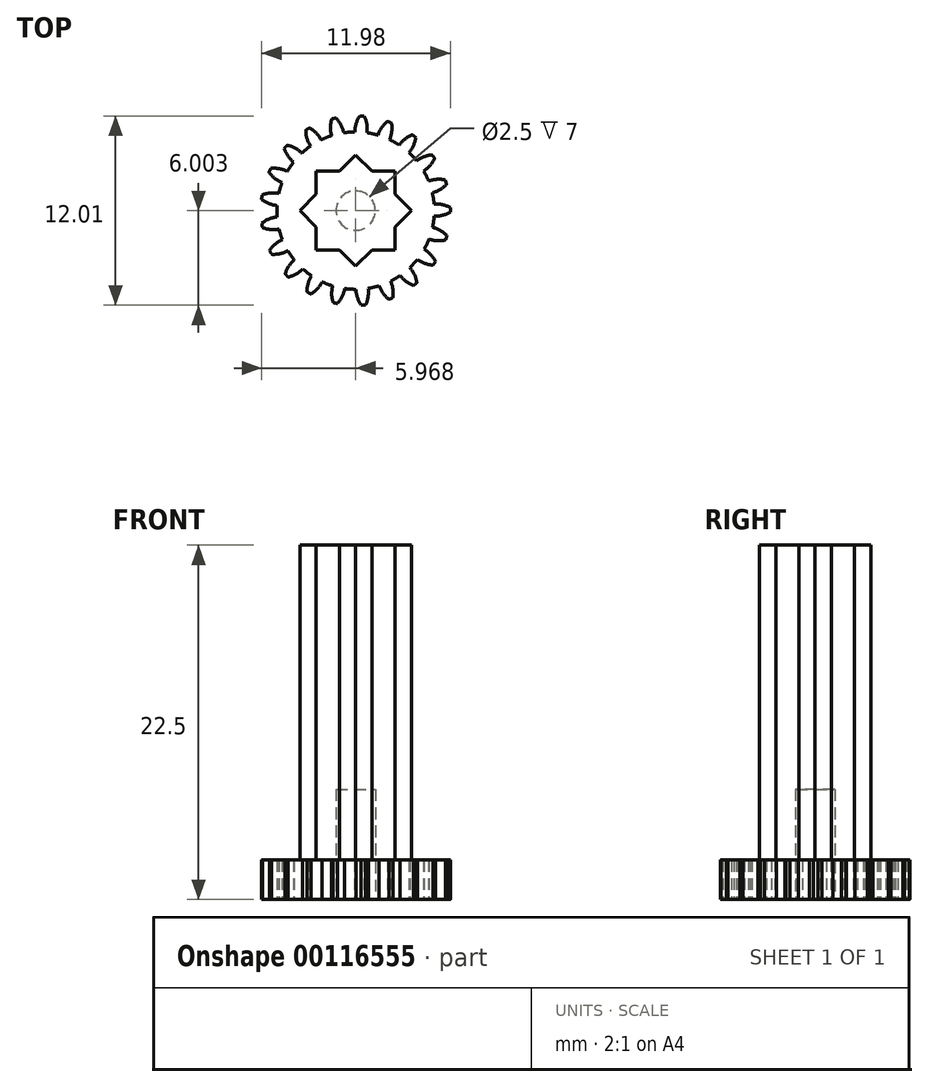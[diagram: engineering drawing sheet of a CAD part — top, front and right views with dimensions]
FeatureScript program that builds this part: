
annotation { "Feature Type Name" : "Feature", "Feature Type Description" : "" }
export const myFeature = defineFeature(function(context is Context, id is Id, definition is map)
    precondition{}
    {
        {
            var Q0;
            Q0=qCreatedBy(makeId("Top.planeOp"),FACE);
            var sketch = newSketch(context, id + "F0", { "sketchPlane" : qUnion([Q0])});
            skLineSegment(sketch, "E0", {"start": v(61.42, 3.14) * mm, "end": v(65.52, 3.14) * mm, "construction": true});
            skLineSegment(sketch, "E1", {"start": v(61.42, 3.14) * mm, "end": v(65.31, 4.4) * mm, "construction": true});
            skLineSegment(sketch, "E2", {"start": v(61.42, 3.14) * mm, "end": v(65.72, 3.82) * mm, "construction": true});
            skPoint(sketch, "E3.third.point", {"position": v(57.79, 0) * mm});
            skArc(sketch, "E4.MirrorCS", {"start": v(62.86, 3.22) * mm, "mid": v(63.38, 3.1) * mm, "end": v(63.92, 3.14) * mm});
            skArc(sketch, "E5.MirrorCS", {"start": v(62.86, 3.22) * mm, "mid": v(62.85, 3.3) * mm, "end": v(62.84, 3.36) * mm});
            skArc(sketch, "E6.MirrorCS", {"start": v(62.82, 3.5) * mm, "mid": v(62.83, 3.43) * mm, "end": v(62.84, 3.36) * mm});
            skArc(sketch, "E7.MirrorCS", {"start": v(62.82, 3.5) * mm, "mid": v(63.28, 3.78) * mm, "end": v(63.8, 3.9) * mm});
            skLineSegment(sketch, "E8", {"start": v(68.78, 4.3) * mm, "end": v(63.8, 3.9) * mm, "construction": true});
            skArc(sketch, "E9.MirrorCS", {"start": v(63.8, 4.7) * mm, "mid": v(63.78, 4.3) * mm, "end": v(63.8, 3.9) * mm});
            skArc(sketch, "E10.1.0", {"start": v(63.44, 1.53) * mm, "mid": v(63.98, 1.57) * mm, "end": v(64.48, 1.76) * mm});
            skArc(sketch, "E10.1.1", {"start": v(63.32, 1.78) * mm, "mid": v(63.35, 1.72) * mm, "end": v(63.38, 1.65) * mm});
            skArc(sketch, "E10.1.2", {"start": v(63.44, 1.53) * mm, "mid": v(63.4, 1.6) * mm, "end": v(63.38, 1.65) * mm});
            skArc(sketch, "E10.1.3", {"start": v(63.32, 1.78) * mm, "mid": v(63.68, 2.18) * mm, "end": v(64.13, 2.46) * mm});
            skArc(sketch, "E10.1.4", {"start": v(63.9, 3.2) * mm, "mid": v(64, 2.83) * mm, "end": v(64.13, 2.46) * mm});
            skArc(sketch, "E10.2.0", {"start": v(64.5, 0.08) * mm, "mid": v(65, 0.27) * mm, "end": v(65.42, 0.6) * mm});
            skArc(sketch, "E10.2.1", {"start": v(64.3, 0.28) * mm, "mid": v(64.35, 0.23) * mm, "end": v(64.4, 0.18) * mm});
            skArc(sketch, "E10.2.2", {"start": v(64.5, 0.08) * mm, "mid": v(64.45, 0.13) * mm, "end": v(64.4, 0.18) * mm});
            skArc(sketch, "E10.2.3", {"start": v(64.3, 0.28) * mm, "mid": v(64.53, 0.77) * mm, "end": v(64.88, 1.17) * mm});
            skArc(sketch, "E10.2.4", {"start": v(64.44, 1.82) * mm, "mid": v(64.65, 1.48) * mm, "end": v(64.88, 1.17) * mm});
            skArc(sketch, "E10.3.0", {"start": v(65.93, -1) * mm, "mid": v(66.35, -0.66) * mm, "end": v(66.66, -0.23) * mm});
            skArc(sketch, "E10.3.1", {"start": v(65.69, -0.86) * mm, "mid": v(65.75, -0.9) * mm, "end": v(65.8, -0.93) * mm});
            skArc(sketch, "E10.3.2", {"start": v(65.93, -1) * mm, "mid": v(65.87, -0.96) * mm, "end": v(65.8, -0.93) * mm});
            skArc(sketch, "E10.3.3", {"start": v(65.69, -0.86) * mm, "mid": v(65.76, -0.33) * mm, "end": v(65.98, 0.16) * mm});
            skArc(sketch, "E10.3.4", {"start": v(65.37, 0.65) * mm, "mid": v(65.66, 0.4) * mm, "end": v(65.98, 0.16) * mm});
            skArc(sketch, "E10.4.0", {"start": v(67.62, -1.6) * mm, "mid": v(67.92, -1.16) * mm, "end": v(68.09, -0.65) * mm});
            skArc(sketch, "E10.4.1", {"start": v(67.35, -1.54) * mm, "mid": v(67.42, -1.56) * mm, "end": v(67.48, -1.57) * mm});
            skArc(sketch, "E10.4.2", {"start": v(67.62, -1.6) * mm, "mid": v(67.55, -1.59) * mm, "end": v(67.48, -1.57) * mm});
            skArc(sketch, "E10.4.3", {"start": v(67.35, -1.54) * mm, "mid": v(67.26, -1.01) * mm, "end": v(67.32, -0.48) * mm});
            skArc(sketch, "E10.4.4", {"start": v(66.6, -0.2) * mm, "mid": v(66.95, -0.35) * mm, "end": v(67.32, -0.48) * mm});
            skArc(sketch, "E10.5.0", {"start": v(69.41, -1.68) * mm, "mid": v(69.57, -1.17) * mm, "end": v(69.58, -0.63) * mm});
            skArc(sketch, "E10.5.1", {"start": v(69.13, -1.7) * mm, "mid": v(69.2, -1.7) * mm, "end": v(69.27, -1.7) * mm});
            skArc(sketch, "E10.5.2", {"start": v(69.41, -1.68) * mm, "mid": v(69.34, -1.69) * mm, "end": v(69.27, -1.7) * mm});
            skArc(sketch, "E10.5.3", {"start": v(69.13, -1.7) * mm, "mid": v(68.9, -1.22) * mm, "end": v(68.8, -0.7) * mm});
            skArc(sketch, "E10.5.4", {"start": v(68.02, -0.64) * mm, "mid": v(68.4, -0.68) * mm, "end": v(68.8, -0.7) * mm});
            skArc(sketch, "E10.6.0", {"start": v(71.15, -1.23) * mm, "mid": v(71.15, -0.7) * mm, "end": v(71, -0.18) * mm});
            skArc(sketch, "E10.6.1", {"start": v(70.89, -1.33) * mm, "mid": v(70.95, -1.3) * mm, "end": v(71.02, -1.28) * mm});
            skArc(sketch, "E10.6.2", {"start": v(71.15, -1.23) * mm, "mid": v(71.08, -1.25) * mm, "end": v(71.02, -1.28) * mm});
            skArc(sketch, "E10.6.3", {"start": v(70.89, -1.33) * mm, "mid": v(70.52, -0.94) * mm, "end": v(70.27, -0.47) * mm});
            skArc(sketch, "E10.6.4", {"start": v(69.5, -0.64) * mm, "mid": v(69.9, -0.57) * mm, "end": v(70.27, -0.47) * mm});
            skArc(sketch, "E10.7.0", {"start": v(72.67, -0.28) * mm, "mid": v(72.51, 0.23) * mm, "end": v(72.22, 0.68) * mm});
            skArc(sketch, "E10.7.1", {"start": v(72.45, -0.46) * mm, "mid": v(72.5, -0.42) * mm, "end": v(72.56, -0.37) * mm});
            skArc(sketch, "E10.7.2", {"start": v(72.67, -0.28) * mm, "mid": v(72.62, -0.33) * mm, "end": v(72.56, -0.37) * mm});
            skArc(sketch, "E10.7.3", {"start": v(72.45, -0.46) * mm, "mid": v(71.99, -0.2) * mm, "end": v(71.61, 0.18) * mm});
            skArc(sketch, "E10.7.4", {"start": v(70.93, -0.2) * mm, "mid": v(71.28, -0.03) * mm, "end": v(71.61, 0.18) * mm});
            skArc(sketch, "E10.8.0", {"start": v(73.85, 1.07) * mm, "mid": v(73.55, 1.51) * mm, "end": v(73.14, 1.85) * mm});
            skArc(sketch, "E10.8.1", {"start": v(73.7, 0.84) * mm, "mid": v(73.73, 0.9) * mm, "end": v(73.77, 0.95) * mm});
            skArc(sketch, "E10.8.2", {"start": v(73.85, 1.07) * mm, "mid": v(73.81, 1.01) * mm, "end": v(73.77, 0.95) * mm});
            skArc(sketch, "E10.8.3", {"start": v(73.7, 0.84) * mm, "mid": v(73.17, 0.95) * mm, "end": v(72.7, 1.2) * mm});
            skArc(sketch, "E10.8.4", {"start": v(72.17, 0.63) * mm, "mid": v(72.44, 0.9) * mm, "end": v(72.7, 1.2) * mm});
            skArc(sketch, "E10.9.0", {"start": v(74.58, 2.7) * mm, "mid": v(74.16, 3.04) * mm, "end": v(73.66, 3.24) * mm});
            skArc(sketch, "E10.9.1", {"start": v(74.5, 2.44) * mm, "mid": v(74.52, 2.5) * mm, "end": v(74.54, 2.57) * mm});
            skArc(sketch, "E10.9.2", {"start": v(74.58, 2.7) * mm, "mid": v(74.56, 2.64) * mm, "end": v(74.54, 2.57) * mm});
            skArc(sketch, "E10.9.3", {"start": v(74.5, 2.44) * mm, "mid": v(73.96, 2.4) * mm, "end": v(73.44, 2.5) * mm});
            skArc(sketch, "E10.9.4", {"start": v(73.1, 1.8) * mm, "mid": v(73.28, 2.14) * mm, "end": v(73.44, 2.5) * mm});
            skArc(sketch, "E10.10.0", {"start": v(74.79, 4.49) * mm, "mid": v(74.3, 4.68) * mm, "end": v(73.76, 4.73) * mm});
            skArc(sketch, "E10.10.1", {"start": v(74.8, 4.2) * mm, "mid": v(74.8, 4.28) * mm, "end": v(74.8, 4.35) * mm});
            skArc(sketch, "E10.10.2", {"start": v(74.79, 4.49) * mm, "mid": v(74.8, 4.42) * mm, "end": v(74.8, 4.35) * mm});
            skArc(sketch, "E10.10.3", {"start": v(74.8, 4.2) * mm, "mid": v(74.3, 4) * mm, "end": v(73.77, 3.95) * mm});
            skArc(sketch, "E10.10.4", {"start": v(73.65, 3.18) * mm, "mid": v(73.72, 3.56) * mm, "end": v(73.77, 3.95) * mm});
            skArc(sketch, "E10.11.0", {"start": v(74.47, 6.25) * mm, "mid": v(73.93, 6.3) * mm, "end": v(73.41, 6.18) * mm});
            skArc(sketch, "E10.11.1", {"start": v(74.55, 5.99) * mm, "mid": v(74.53, 6.05) * mm, "end": v(74.51, 6.12) * mm});
            skArc(sketch, "E10.11.2", {"start": v(74.47, 6.25) * mm, "mid": v(74.5, 6.19) * mm, "end": v(74.51, 6.12) * mm});
            skArc(sketch, "E10.11.3", {"start": v(74.55, 5.99) * mm, "mid": v(74.14, 5.64) * mm, "end": v(73.65, 5.44) * mm});
            skArc(sketch, "E10.11.4", {"start": v(73.77, 4.66) * mm, "mid": v(73.72, 5.05) * mm, "end": v(73.65, 5.44) * mm});
            skArc(sketch, "E10.12.0", {"start": v(73.64, 7.84) * mm, "mid": v(73.12, 7.72) * mm, "end": v(72.65, 7.46) * mm});
            skArc(sketch, "E10.12.1", {"start": v(73.8, 7.61) * mm, "mid": v(73.76, 7.67) * mm, "end": v(73.72, 7.73) * mm});
            skArc(sketch, "E10.12.2", {"start": v(73.64, 7.84) * mm, "mid": v(73.68, 7.79) * mm, "end": v(73.72, 7.73) * mm});
            skArc(sketch, "E10.12.3", {"start": v(73.8, 7.61) * mm, "mid": v(73.5, 7.17) * mm, "end": v(73.1, 6.82) * mm});
            skArc(sketch, "E10.12.4", {"start": v(73.44, 6.12) * mm, "mid": v(73.28, 6.47) * mm, "end": v(73.1, 6.82) * mm});
            skArc(sketch, "E10.13.0", {"start": v(72.38, 9.12) * mm, "mid": v(71.92, 8.85) * mm, "end": v(71.55, 8.46) * mm});
            skArc(sketch, "E10.13.1", {"start": v(72.6, 8.95) * mm, "mid": v(72.55, 9) * mm, "end": v(72.5, 9.03) * mm});
            skArc(sketch, "E10.13.2", {"start": v(72.38, 9.12) * mm, "mid": v(72.44, 9.08) * mm, "end": v(72.5, 9.03) * mm});
            skArc(sketch, "E10.13.3", {"start": v(72.6, 8.95) * mm, "mid": v(72.45, 8.43) * mm, "end": v(72.16, 7.98) * mm});
            skArc(sketch, "E10.13.4", {"start": v(72.7, 7.4) * mm, "mid": v(72.44, 7.7) * mm, "end": v(72.16, 7.98) * mm});
            skArc(sketch, "E10.14.0", {"start": v(70.8, 9.97) * mm, "mid": v(70.44, 9.58) * mm, "end": v(70.2, 9.1) * mm});
            skArc(sketch, "E10.14.1", {"start": v(71.06, 9.87) * mm, "mid": v(71, 9.9) * mm, "end": v(70.93, 9.92) * mm});
            skArc(sketch, "E10.14.2", {"start": v(70.8, 9.97) * mm, "mid": v(70.87, 9.94) * mm, "end": v(70.93, 9.92) * mm});
            skArc(sketch, "E10.14.3", {"start": v(71.06, 9.87) * mm, "mid": v(71.07, 9.33) * mm, "end": v(70.93, 8.82) * mm});
            skArc(sketch, "E10.14.4", {"start": v(71.6, 8.43) * mm, "mid": v(71.28, 8.63) * mm, "end": v(70.93, 8.82) * mm});
            skArc(sketch, "E10.15.0", {"start": v(69.04, 10.31) * mm, "mid": v(68.81, 9.83) * mm, "end": v(68.72, 9.3) * mm});
            skArc(sketch, "E10.15.1", {"start": v(69.32, 10.3) * mm, "mid": v(69.25, 10.3) * mm, "end": v(69.18, 10.3) * mm});
            skArc(sketch, "E10.15.2", {"start": v(69.04, 10.31) * mm, "mid": v(69.11, 10.3) * mm, "end": v(69.18, 10.3) * mm});
            skArc(sketch, "E10.15.3", {"start": v(69.32, 10.3) * mm, "mid": v(69.49, 9.78) * mm, "end": v(69.5, 9.25) * mm});
            skArc(sketch, "E10.15.4", {"start": v(70.27, 9.08) * mm, "mid": v(69.89, 9.18) * mm, "end": v(69.5, 9.25) * mm});
            skArc(sketch, "E10.16.0", {"start": v(67.26, 10.12) * mm, "mid": v(67.18, 9.6) * mm, "end": v(67.25, 9.06) * mm});
            skArc(sketch, "E10.16.1", {"start": v(67.53, 10.19) * mm, "mid": v(67.46, 10.17) * mm, "end": v(67.4, 10.16) * mm});
            skArc(sketch, "E10.16.2", {"start": v(67.26, 10.12) * mm, "mid": v(67.33, 10.14) * mm, "end": v(67.4, 10.16) * mm});
            skArc(sketch, "E10.16.3", {"start": v(67.53, 10.19) * mm, "mid": v(67.84, 9.75) * mm, "end": v(68.01, 9.24) * mm});
            skArc(sketch, "E10.16.4", {"start": v(68.8, 9.3) * mm, "mid": v(68.4, 9.29) * mm, "end": v(68.01, 9.24) * mm});
            skArc(sketch, "E10.17.0", {"start": v(65.61, 9.42) * mm, "mid": v(65.7, 8.89) * mm, "end": v(65.92, 8.4) * mm});
            skArc(sketch, "E10.17.1", {"start": v(65.85, 9.56) * mm, "mid": v(65.8, 9.52) * mm, "end": v(65.73, 9.49) * mm});
            skArc(sketch, "E10.17.2", {"start": v(65.61, 9.42) * mm, "mid": v(65.67, 9.45) * mm, "end": v(65.73, 9.49) * mm});
            skArc(sketch, "E10.17.3", {"start": v(65.85, 9.56) * mm, "mid": v(66.28, 9.23) * mm, "end": v(66.6, 8.8) * mm});
            skArc(sketch, "E10.17.4", {"start": v(67.32, 9.09) * mm, "mid": v(66.95, 8.96) * mm, "end": v(66.6, 8.8) * mm});
            skArc(sketch, "E10.18.0", {"start": v(64.25, 8.26) * mm, "mid": v(64.48, 7.77) * mm, "end": v(64.83, 7.38) * mm});
            skArc(sketch, "E10.18.1", {"start": v(64.43, 8.46) * mm, "mid": v(64.39, 8.41) * mm, "end": v(64.34, 8.36) * mm});
            skArc(sketch, "E10.18.2", {"start": v(64.25, 8.26) * mm, "mid": v(64.3, 8.3) * mm, "end": v(64.34, 8.36) * mm});
            skArc(sketch, "E10.18.3", {"start": v(64.43, 8.46) * mm, "mid": v(64.93, 8.28) * mm, "end": v(65.36, 7.95) * mm});
            skArc(sketch, "E10.18.4", {"start": v(65.97, 8.44) * mm, "mid": v(65.66, 8.21) * mm, "end": v(65.36, 7.95) * mm});
            skArc(sketch, "E10.19.0", {"start": v(63.28, 6.75) * mm, "mid": v(63.64, 6.35) * mm, "end": v(64.1, 6.08) * mm});
            skArc(sketch, "E10.19.1", {"start": v(63.4, 7) * mm, "mid": v(63.37, 6.94) * mm, "end": v(63.34, 6.87) * mm});
            skArc(sketch, "E10.19.2", {"start": v(63.28, 6.75) * mm, "mid": v(63.3, 6.8) * mm, "end": v(63.34, 6.87) * mm});
            skArc(sketch, "E10.19.3", {"start": v(63.4, 7) * mm, "mid": v(63.93, 6.97) * mm, "end": v(64.44, 6.79) * mm});
            skArc(sketch, "E10.19.4", {"start": v(64.88, 7.43) * mm, "mid": v(64.65, 7.12) * mm, "end": v(64.44, 6.79) * mm});
            skArc(sketch, "E11.4.20.0", {"start": v(62.85, 5.3) * mm, "mid": v(62.83, 5.22) * mm, "end": v(62.82, 5.16) * mm});
            skArc(sketch, "E11.8.20.0", {"start": v(62.8, 5.02) * mm, "mid": v(62.81, 5.09) * mm, "end": v(62.82, 5.16) * mm});
            skArc(sketch, "E11.12.20.0", {"start": v(62.85, 5.3) * mm, "mid": v(63.36, 5.42) * mm, "end": v(63.9, 5.4) * mm});
            skArc(sketch, "E11.15.20.0", {"start": v(62.8, 5.02) * mm, "mid": v(63.27, 4.75) * mm, "end": v(63.79, 4.62) * mm});
            skArc(sketch, "E11.16.20.0", {"start": v(64.13, 6.14) * mm, "mid": v(64, 5.77) * mm, "end": v(63.9, 5.4) * mm});
            skSolve(sketch);
        }
        {
            var Q0;
            Q0 = qSketchRegion(id + "F0", true);
            extrude(context, id + "F1", {"entities" : qUnion([Q0]), "depth" : 2.5 * mm});
        }
        {
            var Q0;
            Q0=makeQuery(id+"F1.opExtrude","CAP_FACE",FACE,{"disambiguationData":[OSD([sQuery(id+"F0.wireOp",EDGE,"E4.MirrorCS"),sQuery(id+"F0.wireOp",EDGE,"E5.MirrorCS"),sQuery(id+"F0.wireOp",EDGE,"E6.MirrorCS"),sQuery(id+"F0.wireOp",EDGE,"E7.MirrorCS"),sQuery(id+"F0.wireOp",EDGE,"E9.MirrorCS"),sQuery(id+"F0.wireOp",EDGE,"E10.1.0"),sQuery(id+"F0.wireOp",EDGE,"E10.1.1"),sQuery(id+"F0.wireOp",EDGE,"E10.1.2"),sQuery(id+"F0.wireOp",EDGE,"E10.1.3"),sQuery(id+"F0.wireOp",EDGE,"E10.1.4"),sQuery(id+"F0.wireOp",EDGE,"E10.2.0"),sQuery(id+"F0.wireOp",EDGE,"E10.2.1"),sQuery(id+"F0.wireOp",EDGE,"E10.2.2"),sQuery(id+"F0.wireOp",EDGE,"E10.2.3"),sQuery(id+"F0.wireOp",EDGE,"E10.2.4"),sQuery(id+"F0.wireOp",EDGE,"E10.3.0"),sQuery(id+"F0.wireOp",EDGE,"E10.3.1"),sQuery(id+"F0.wireOp",EDGE,"E10.3.2"),sQuery(id+"F0.wireOp",EDGE,"E10.3.3"),sQuery(id+"F0.wireOp",EDGE,"E10.3.4"),sQuery(id+"F0.wireOp",EDGE,"E10.4.0"),sQuery(id+"F0.wireOp",EDGE,"E10.4.1"),sQuery(id+"F0.wireOp",EDGE,"E10.4.2"),sQuery(id+"F0.wireOp",EDGE,"E10.4.3"),sQuery(id+"F0.wireOp",EDGE,"E10.4.4"),sQuery(id+"F0.wireOp",EDGE,"E10.5.0"),sQuery(id+"F0.wireOp",EDGE,"E10.5.1"),sQuery(id+"F0.wireOp",EDGE,"E10.5.2"),sQuery(id+"F0.wireOp",EDGE,"E10.5.3"),sQuery(id+"F0.wireOp",EDGE,"E10.5.4"),sQuery(id+"F0.wireOp",EDGE,"E10.6.0"),sQuery(id+"F0.wireOp",EDGE,"E10.6.1"),sQuery(id+"F0.wireOp",EDGE,"E10.6.2"),sQuery(id+"F0.wireOp",EDGE,"E10.6.3"),sQuery(id+"F0.wireOp",EDGE,"E10.6.4"),sQuery(id+"F0.wireOp",EDGE,"E10.7.0"),sQuery(id+"F0.wireOp",EDGE,"E10.7.1"),sQuery(id+"F0.wireOp",EDGE,"E10.7.2"),sQuery(id+"F0.wireOp",EDGE,"E10.7.3"),sQuery(id+"F0.wireOp",EDGE,"E10.7.4"),sQuery(id+"F0.wireOp",EDGE,"E10.8.0"),sQuery(id+"F0.wireOp",EDGE,"E10.8.1"),sQuery(id+"F0.wireOp",EDGE,"E10.8.2"),sQuery(id+"F0.wireOp",EDGE,"E10.8.3"),sQuery(id+"F0.wireOp",EDGE,"E10.8.4"),sQuery(id+"F0.wireOp",EDGE,"E10.9.0"),sQuery(id+"F0.wireOp",EDGE,"E10.9.1"),sQuery(id+"F0.wireOp",EDGE,"E10.9.2"),sQuery(id+"F0.wireOp",EDGE,"E10.9.3"),sQuery(id+"F0.wireOp",EDGE,"E10.9.4"),sQuery(id+"F0.wireOp",EDGE,"E10.10.0"),sQuery(id+"F0.wireOp",EDGE,"E10.10.1"),sQuery(id+"F0.wireOp",EDGE,"E10.10.2"),sQuery(id+"F0.wireOp",EDGE,"E10.10.3"),sQuery(id+"F0.wireOp",EDGE,"E10.10.4"),sQuery(id+"F0.wireOp",EDGE,"E10.11.0"),sQuery(id+"F0.wireOp",EDGE,"E10.11.1"),sQuery(id+"F0.wireOp",EDGE,"E10.11.2"),sQuery(id+"F0.wireOp",EDGE,"E10.11.3"),sQuery(id+"F0.wireOp",EDGE,"E10.11.4"),sQuery(id+"F0.wireOp",EDGE,"E10.12.0"),sQuery(id+"F0.wireOp",EDGE,"E10.12.1"),sQuery(id+"F0.wireOp",EDGE,"E10.12.2"),sQuery(id+"F0.wireOp",EDGE,"E10.12.3"),sQuery(id+"F0.wireOp",EDGE,"E10.12.4"),sQuery(id+"F0.wireOp",EDGE,"E10.13.0"),sQuery(id+"F0.wireOp",EDGE,"E10.13.1"),sQuery(id+"F0.wireOp",EDGE,"E10.13.2"),sQuery(id+"F0.wireOp",EDGE,"E10.13.3"),sQuery(id+"F0.wireOp",EDGE,"E10.13.4"),sQuery(id+"F0.wireOp",EDGE,"E10.14.0"),sQuery(id+"F0.wireOp",EDGE,"E10.14.1"),sQuery(id+"F0.wireOp",EDGE,"E10.14.2"),sQuery(id+"F0.wireOp",EDGE,"E10.14.3"),sQuery(id+"F0.wireOp",EDGE,"E10.14.4"),sQuery(id+"F0.wireOp",EDGE,"E10.15.0"),sQuery(id+"F0.wireOp",EDGE,"E10.15.1"),sQuery(id+"F0.wireOp",EDGE,"E10.15.2"),sQuery(id+"F0.wireOp",EDGE,"E10.15.3"),sQuery(id+"F0.wireOp",EDGE,"E10.15.4"),sQuery(id+"F0.wireOp",EDGE,"E10.16.0"),sQuery(id+"F0.wireOp",EDGE,"E10.16.1"),sQuery(id+"F0.wireOp",EDGE,"E10.16.2"),sQuery(id+"F0.wireOp",EDGE,"E10.16.3"),sQuery(id+"F0.wireOp",EDGE,"E10.16.4"),sQuery(id+"F0.wireOp",EDGE,"E10.17.0"),sQuery(id+"F0.wireOp",EDGE,"E10.17.1"),sQuery(id+"F0.wireOp",EDGE,"E10.17.2"),sQuery(id+"F0.wireOp",EDGE,"E10.17.3"),sQuery(id+"F0.wireOp",EDGE,"E10.17.4"),sQuery(id+"F0.wireOp",EDGE,"E10.18.0"),sQuery(id+"F0.wireOp",EDGE,"E10.18.1"),sQuery(id+"F0.wireOp",EDGE,"E10.18.2"),sQuery(id+"F0.wireOp",EDGE,"E10.18.3"),sQuery(id+"F0.wireOp",EDGE,"E10.18.4"),sQuery(id+"F0.wireOp",EDGE,"E10.19.0"),sQuery(id+"F0.wireOp",EDGE,"E10.19.1"),sQuery(id+"F0.wireOp",EDGE,"E10.19.2"),sQuery(id+"F0.wireOp",EDGE,"E10.19.3"),sQuery(id+"F0.wireOp",EDGE,"E10.19.4"),sQuery(id+"F0.wireOp",EDGE,"E11.4.20.0"),sQuery(id+"F0.wireOp",EDGE,"E11.8.20.0"),sQuery(id+"F0.wireOp",EDGE,"E11.12.20.0"),sQuery(id+"F0.wireOp",EDGE,"E11.15.20.0"),sQuery(id+"F0.wireOp",EDGE,"E11.16.20.0")])],"isStart":false});
            var sketch = newSketch(context, id + "F2", { "sketchPlane" : qUnion([Q0])});
            skLineSegment(sketch, "E12.bottom", {"start": v(71.28, 1.8) * mm, "end": v(66.28, 1.8) * mm});
            skLineSegment(sketch, "E12.top", {"start": v(71.28, 6.8) * mm, "end": v(66.28, 6.8) * mm});
            skLineSegment(sketch, "E12.left", {"start": v(71.28, 1.8) * mm, "end": v(71.28, 6.8) * mm});
            skLineSegment(sketch, "E12.right", {"start": v(66.28, 1.8) * mm, "end": v(66.28, 6.8) * mm});
            skPoint(sketch, "E12.middle", {"position": v(68.78, 4.3) * mm});
            skLineSegment(sketch, "E13", {"start": v(65.24, 4.3) * mm, "end": v(68.78, 7.84) * mm});
            skLineSegment(sketch, "E14", {"start": v(68.78, 7.84) * mm, "end": v(72.31, 4.3) * mm});
            skLineSegment(sketch, "E15", {"start": v(72.31, 4.3) * mm, "end": v(68.78, 0.77) * mm});
            skLineSegment(sketch, "E16", {"start": v(68.78, 0.77) * mm, "end": v(65.24, 4.3) * mm});
            skSolve(sketch);
        }
        {
            var Q0;
            Q0 = qSketchRegion(id + "F2", true);
            extrude(context, id + "F3", {"entities" : qUnion([Q0]), "operationType" : NewBodyOperationType.ADD, "depth" : 20 * mm});
        }
        {
            var Q0;
            Q0=makeQuery(id+"F1.opExtrude","CAP_FACE",FACE,{"disambiguationData":[OSD([sQuery(id+"F0.wireOp",EDGE,"E4.MirrorCS"),sQuery(id+"F0.wireOp",EDGE,"E5.MirrorCS"),sQuery(id+"F0.wireOp",EDGE,"E6.MirrorCS"),sQuery(id+"F0.wireOp",EDGE,"E7.MirrorCS"),sQuery(id+"F0.wireOp",EDGE,"E9.MirrorCS"),sQuery(id+"F0.wireOp",EDGE,"E10.1.0"),sQuery(id+"F0.wireOp",EDGE,"E10.1.1"),sQuery(id+"F0.wireOp",EDGE,"E10.1.2"),sQuery(id+"F0.wireOp",EDGE,"E10.1.3"),sQuery(id+"F0.wireOp",EDGE,"E10.1.4"),sQuery(id+"F0.wireOp",EDGE,"E10.2.0"),sQuery(id+"F0.wireOp",EDGE,"E10.2.1"),sQuery(id+"F0.wireOp",EDGE,"E10.2.2"),sQuery(id+"F0.wireOp",EDGE,"E10.2.3"),sQuery(id+"F0.wireOp",EDGE,"E10.2.4"),sQuery(id+"F0.wireOp",EDGE,"E10.3.0"),sQuery(id+"F0.wireOp",EDGE,"E10.3.1"),sQuery(id+"F0.wireOp",EDGE,"E10.3.2"),sQuery(id+"F0.wireOp",EDGE,"E10.3.3"),sQuery(id+"F0.wireOp",EDGE,"E10.3.4"),sQuery(id+"F0.wireOp",EDGE,"E10.4.0"),sQuery(id+"F0.wireOp",EDGE,"E10.4.1"),sQuery(id+"F0.wireOp",EDGE,"E10.4.2"),sQuery(id+"F0.wireOp",EDGE,"E10.4.3"),sQuery(id+"F0.wireOp",EDGE,"E10.4.4"),sQuery(id+"F0.wireOp",EDGE,"E10.5.0"),sQuery(id+"F0.wireOp",EDGE,"E10.5.1"),sQuery(id+"F0.wireOp",EDGE,"E10.5.2"),sQuery(id+"F0.wireOp",EDGE,"E10.5.3"),sQuery(id+"F0.wireOp",EDGE,"E10.5.4"),sQuery(id+"F0.wireOp",EDGE,"E10.6.0"),sQuery(id+"F0.wireOp",EDGE,"E10.6.1"),sQuery(id+"F0.wireOp",EDGE,"E10.6.2"),sQuery(id+"F0.wireOp",EDGE,"E10.6.3"),sQuery(id+"F0.wireOp",EDGE,"E10.6.4"),sQuery(id+"F0.wireOp",EDGE,"E10.7.0"),sQuery(id+"F0.wireOp",EDGE,"E10.7.1"),sQuery(id+"F0.wireOp",EDGE,"E10.7.2"),sQuery(id+"F0.wireOp",EDGE,"E10.7.3"),sQuery(id+"F0.wireOp",EDGE,"E10.7.4"),sQuery(id+"F0.wireOp",EDGE,"E10.8.0"),sQuery(id+"F0.wireOp",EDGE,"E10.8.1"),sQuery(id+"F0.wireOp",EDGE,"E10.8.2"),sQuery(id+"F0.wireOp",EDGE,"E10.8.3"),sQuery(id+"F0.wireOp",EDGE,"E10.8.4"),sQuery(id+"F0.wireOp",EDGE,"E10.9.0"),sQuery(id+"F0.wireOp",EDGE,"E10.9.1"),sQuery(id+"F0.wireOp",EDGE,"E10.9.2"),sQuery(id+"F0.wireOp",EDGE,"E10.9.3"),sQuery(id+"F0.wireOp",EDGE,"E10.9.4"),sQuery(id+"F0.wireOp",EDGE,"E10.10.0"),sQuery(id+"F0.wireOp",EDGE,"E10.10.1"),sQuery(id+"F0.wireOp",EDGE,"E10.10.2"),sQuery(id+"F0.wireOp",EDGE,"E10.10.3"),sQuery(id+"F0.wireOp",EDGE,"E10.10.4"),sQuery(id+"F0.wireOp",EDGE,"E10.11.0"),sQuery(id+"F0.wireOp",EDGE,"E10.11.1"),sQuery(id+"F0.wireOp",EDGE,"E10.11.2"),sQuery(id+"F0.wireOp",EDGE,"E10.11.3"),sQuery(id+"F0.wireOp",EDGE,"E10.11.4"),sQuery(id+"F0.wireOp",EDGE,"E10.12.0"),sQuery(id+"F0.wireOp",EDGE,"E10.12.1"),sQuery(id+"F0.wireOp",EDGE,"E10.12.2"),sQuery(id+"F0.wireOp",EDGE,"E10.12.3"),sQuery(id+"F0.wireOp",EDGE,"E10.12.4"),sQuery(id+"F0.wireOp",EDGE,"E10.13.0"),sQuery(id+"F0.wireOp",EDGE,"E10.13.1"),sQuery(id+"F0.wireOp",EDGE,"E10.13.2"),sQuery(id+"F0.wireOp",EDGE,"E10.13.3"),sQuery(id+"F0.wireOp",EDGE,"E10.13.4"),sQuery(id+"F0.wireOp",EDGE,"E10.14.0"),sQuery(id+"F0.wireOp",EDGE,"E10.14.1"),sQuery(id+"F0.wireOp",EDGE,"E10.14.2"),sQuery(id+"F0.wireOp",EDGE,"E10.14.3"),sQuery(id+"F0.wireOp",EDGE,"E10.14.4"),sQuery(id+"F0.wireOp",EDGE,"E10.15.0"),sQuery(id+"F0.wireOp",EDGE,"E10.15.1"),sQuery(id+"F0.wireOp",EDGE,"E10.15.2"),sQuery(id+"F0.wireOp",EDGE,"E10.15.3"),sQuery(id+"F0.wireOp",EDGE,"E10.15.4"),sQuery(id+"F0.wireOp",EDGE,"E10.16.0"),sQuery(id+"F0.wireOp",EDGE,"E10.16.1"),sQuery(id+"F0.wireOp",EDGE,"E10.16.2"),sQuery(id+"F0.wireOp",EDGE,"E10.16.3"),sQuery(id+"F0.wireOp",EDGE,"E10.16.4"),sQuery(id+"F0.wireOp",EDGE,"E10.17.0"),sQuery(id+"F0.wireOp",EDGE,"E10.17.1"),sQuery(id+"F0.wireOp",EDGE,"E10.17.2"),sQuery(id+"F0.wireOp",EDGE,"E10.17.3"),sQuery(id+"F0.wireOp",EDGE,"E10.17.4"),sQuery(id+"F0.wireOp",EDGE,"E10.18.0"),sQuery(id+"F0.wireOp",EDGE,"E10.18.1"),sQuery(id+"F0.wireOp",EDGE,"E10.18.2"),sQuery(id+"F0.wireOp",EDGE,"E10.18.3"),sQuery(id+"F0.wireOp",EDGE,"E10.18.4"),sQuery(id+"F0.wireOp",EDGE,"E10.19.0"),sQuery(id+"F0.wireOp",EDGE,"E10.19.1"),sQuery(id+"F0.wireOp",EDGE,"E10.19.2"),sQuery(id+"F0.wireOp",EDGE,"E10.19.3"),sQuery(id+"F0.wireOp",EDGE,"E10.19.4"),sQuery(id+"F0.wireOp",EDGE,"E11.4.20.0"),sQuery(id+"F0.wireOp",EDGE,"E11.8.20.0"),sQuery(id+"F0.wireOp",EDGE,"E11.12.20.0"),sQuery(id+"F0.wireOp",EDGE,"E11.15.20.0"),sQuery(id+"F0.wireOp",EDGE,"E11.16.20.0")])],"isStart":true});
            var sketch = newSketch(context, id + "F4", { "sketchPlane" : qUnion([Q0])});
            skCircle(sketch, "E17", {"center": v(68.78, -4.3) * mm, "radius": 1.25 * mm});
            skSolve(sketch);
        }
        {
            var Q0;
            Q0 = qSketchRegion(id + "F4", true);
            extrude(context, id + "F5", {"entities" : qUnion([Q0]), "operationType" : NewBodyOperationType.REMOVE, "oppositeDirection" : true, "depth" : 7 * mm});
        }
    });
